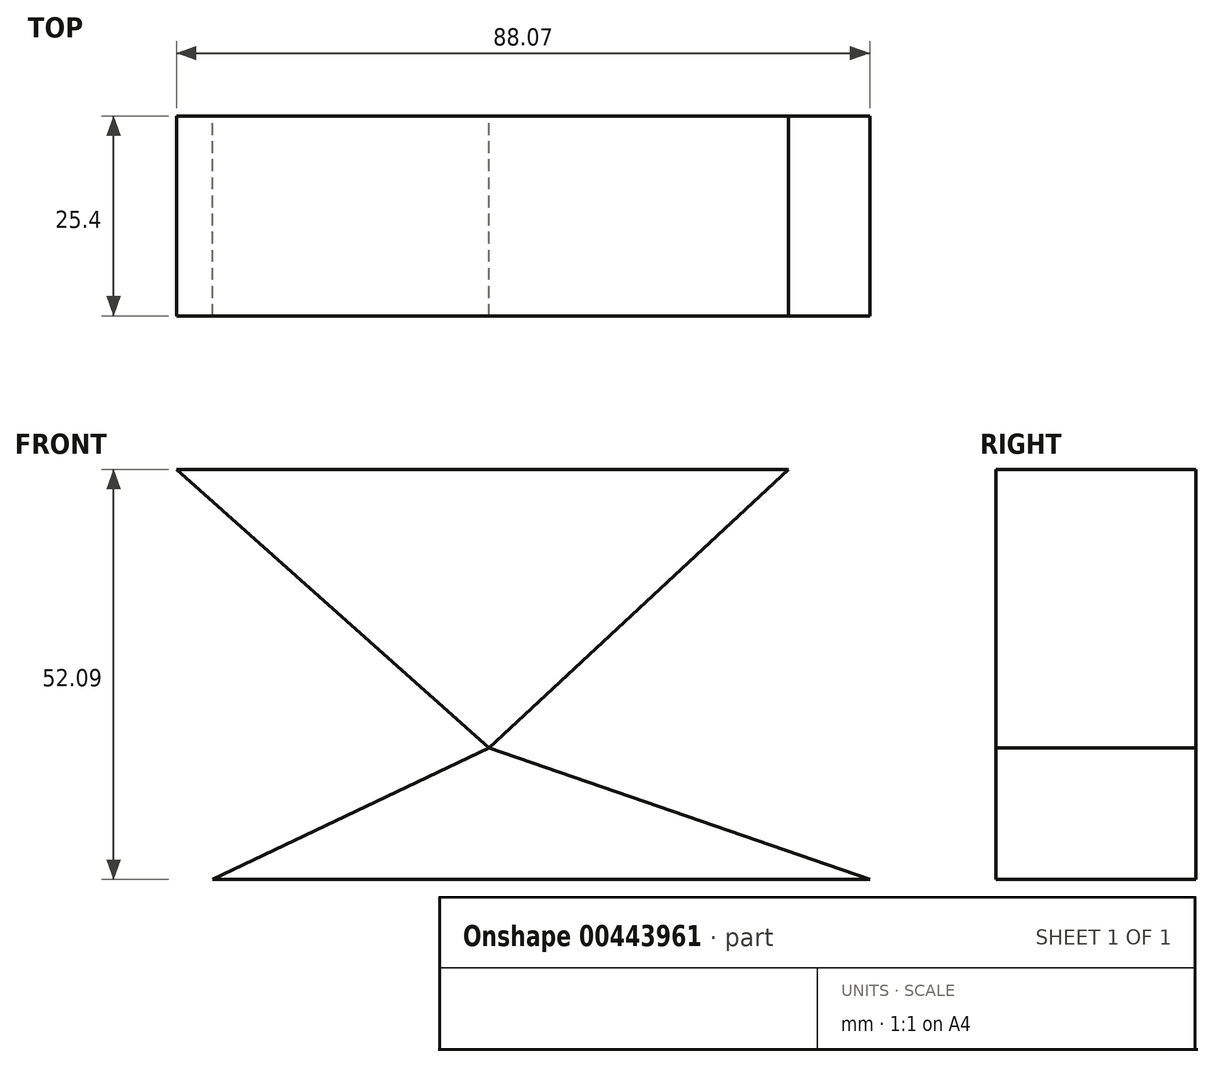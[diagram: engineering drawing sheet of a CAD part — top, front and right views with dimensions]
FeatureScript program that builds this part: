
annotation { "Feature Type Name" : "Feature", "Feature Type Description" : "" }
export const myFeature = defineFeature(function(context is Context, id is Id, definition is map)
    precondition{}
    {
        {
            var Q0;
            Q0=qCreatedBy(makeId("Front.planeOp"),FACE);
            var sketch = newSketch(context, id + "F0", { "sketchPlane" : qUnion([Q0])});
            skLineSegment(sketch, "E0", {"start": v(0, 0) * mm, "end": v(38, 35.4) * mm});
            skLineSegment(sketch, "E1", {"start": v(38, 35.4) * mm, "end": v(-39.72, 35.4) * mm});
            skLineSegment(sketch, "E2", {"start": v(-39.72, 35.4) * mm, "end": v(0, 0) * mm});
            skLineSegment(sketch, "E3", {"start": v(0, 0) * mm, "end": v(48.35, -16.7) * mm});
            skLineSegment(sketch, "E4", {"start": v(48.35, -16.7) * mm, "end": v(-35.11, -16.7) * mm});
            skLineSegment(sketch, "E5", {"start": v(-35.11, -16.7) * mm, "end": v(0, 0) * mm});
            skSolve(sketch);
        }
        {
            var Q0;
            Q0=makeQuery(id+"F0.imprint","IMPRINT",FACE,{"disambiguationData":[TD([[makeQuery(id+"F0.imprint","IMPRINT",EDGE,{"derivedFrom":sQuery(id+"F0.wireOp",EDGE,"E0")}),1.0]])]});
            var Q1;
            Q1=makeQuery(id+"F0.imprint","IMPRINT",FACE,{"disambiguationData":[TD([[makeQuery(id+"F0.imprint","IMPRINT",EDGE,{"derivedFrom":sQuery(id+"F0.wireOp",EDGE,"E3")}),-1.0]])]});
            extrude(context, id + "F1", {"entities" : qUnion([Q0, Q1]), "depth" : 25.4 * mm});
        }
    });
